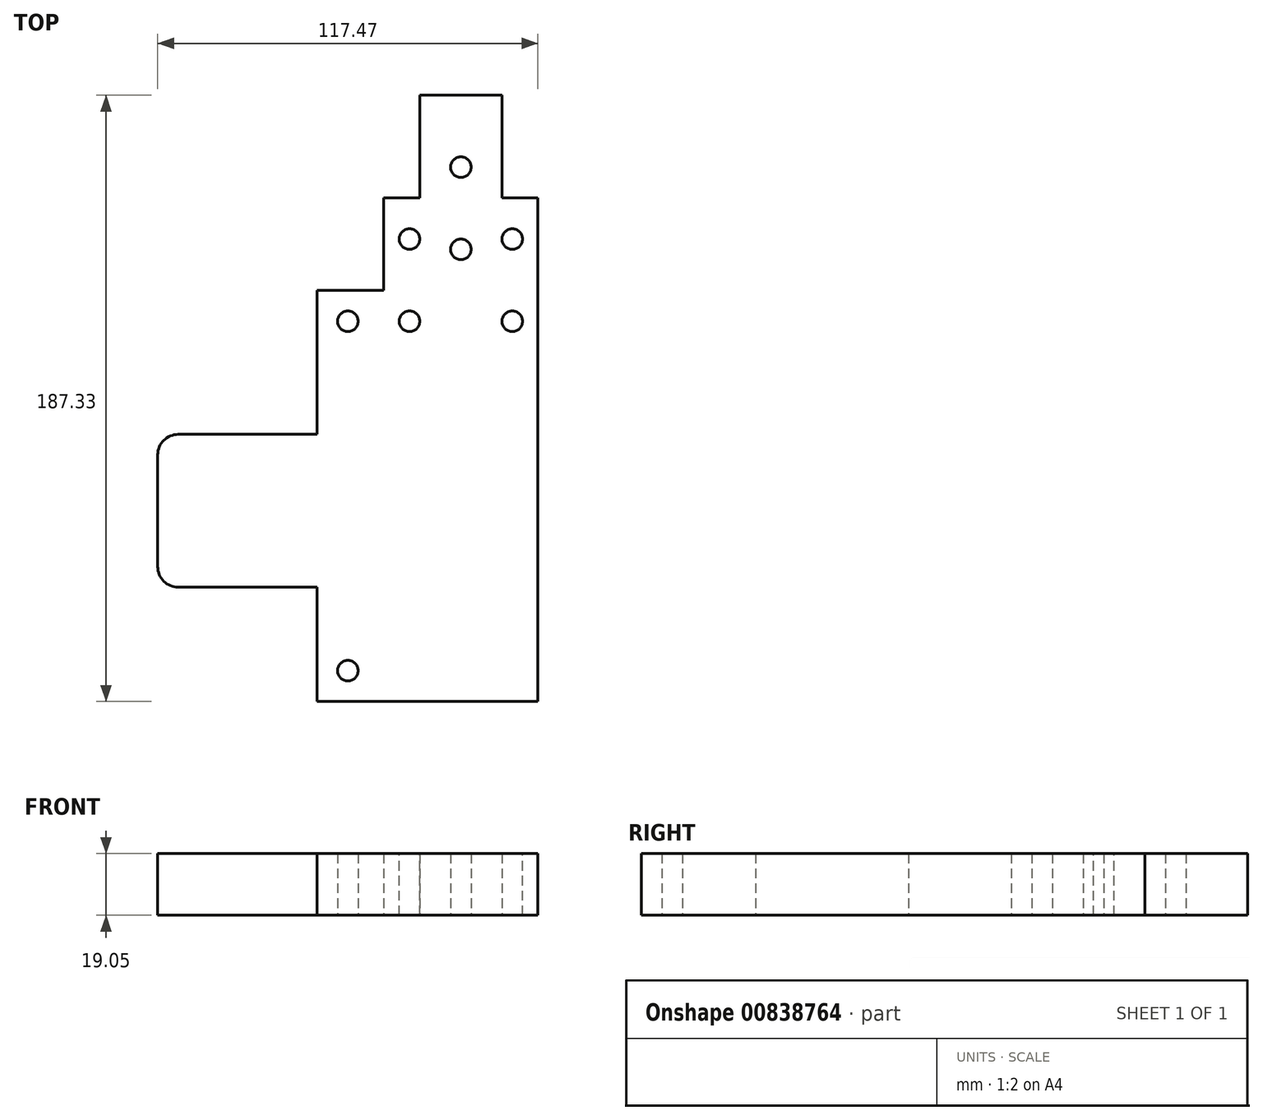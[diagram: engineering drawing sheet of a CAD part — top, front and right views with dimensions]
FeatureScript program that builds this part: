
annotation { "Feature Type Name" : "Feature", "Feature Type Description" : "" }
export const myFeature = defineFeature(function(context is Context, id is Id, definition is map)
    precondition{}
    {
        {
            var Q0;
            Q0=qCreatedBy(makeId("Top.planeOp"),FACE);
            var sketch = newSketch(context, id + "F0", { "sketchPlane" : qUnion([Q0])});
            skLineSegment(sketch, "E0", {"start": v(21.17, -220.11) * mm, "end": v(10.06, -220.11) * mm});
            skLineSegment(sketch, "E1", {"start": v(-26.45, -267.74) * mm, "end": v(-96.3, -267.74) * mm, "construction": true});
            skLineSegment(sketch, "E2", {"start": v(-96.3, -314.98) * mm, "end": v(-26.45, -314.98) * mm});
            skLineSegment(sketch, "E3", {"start": v(-26.45, -220.11) * mm, "end": v(-26.45, -248.69) * mm});
            skLineSegment(sketch, "E4", {"start": v(21.17, -220.11) * mm, "end": v(21.17, -375.69) * mm});
            skLineSegment(sketch, "E5", {"start": v(-26.45, -375.69) * mm, "end": v(21.17, -375.69) * mm});
            skLineSegment(sketch, "E6", {"start": v(-45.5, -340.38) * mm, "end": v(-45.5, -375.69) * mm, "construction": true});
            skLineSegment(sketch, "E7", {"start": v(-26.45, -362.99) * mm, "end": v(-13.75, -362.99) * mm, "construction": true});
            skLineSegment(sketch, "E8", {"start": v(-13.75, -375.69) * mm, "end": v(-13.75, -362.99) * mm});
            skLineSegment(sketch, "E9", {"start": v(-26.45, -350.29) * mm, "end": v(-39.15, -350.29) * mm});
            skLineSegment(sketch, "E10", {"start": v(-26.45, -375.69) * mm, "end": v(-47.09, -375.69) * mm});
            skLineSegment(sketch, "E11", {"start": v(-26.45, -362.99) * mm, "end": v(-26.45, -375.69) * mm});
            skLineSegment(sketch, "E12", {"start": v(-26.45, -340.38) * mm, "end": v(-26.45, -350.29) * mm});
            skLineSegment(sketch, "E13", {"start": v(-96.3, -293.14) * mm, "end": v(-96.3, -340.38) * mm});
            skPoint(sketch, "E14.visualSharp", {"position": v(-45.5, -350.29) * mm});
            skArc(sketch, "E14.filletArc", {"start": v(-39.15, -350.29) * mm, "mid": v(-43.64, -352.15) * mm, "end": v(-45.5, -356.64) * mm});
            skLineSegment(sketch, "E15.top", {"start": v(-15.34, -213.76) * mm, "end": v(10.06, -213.76) * mm, "construction": true});
            skLineSegment(sketch, "E15.left", {"start": v(-15.34, -220.11) * mm, "end": v(-15.34, -188.36) * mm});
            skLineSegment(sketch, "E15.right", {"start": v(10.06, -220.11) * mm, "end": v(10.06, -188.36) * mm});
            skLineSegment(sketch, "E16.trimOffspring", {"start": v(-15.34, -220.11) * mm, "end": v(-26.45, -220.11) * mm});
            skLineSegment(sketch, "E17.0", {"start": v(-96.3, -340.38) * mm, "end": v(-47.09, -340.38) * mm});
            skLineSegment(sketch, "E18.0", {"start": v(-26.45, -293.14) * mm, "end": v(-47.09, -293.14) * mm, "construction": true});
            skLineSegment(sketch, "E19.0", {"start": v(-15.34, -188.36) * mm, "end": v(10.06, -188.36) * mm});
            skCircle(sketch, "E20", {"center": v(-37.56, -366.16) * mm, "radius": 3.18 * mm});
            skLineSegment(sketch, "E21.0", {"start": v(-47.09, -242.34) * mm, "end": v(-47.09, -245.51) * mm, "construction": true});
            skLineSegment(sketch, "E22.0", {"start": v(-26.45, -242.34) * mm, "end": v(-47.09, -242.34) * mm, "construction": true});
            skLineSegment(sketch, "E23.trimOffspring", {"start": v(-47.09, -340.38) * mm, "end": v(-47.09, -375.69) * mm});
            skLineSegment(sketch, "E24", {"start": v(-47.09, -293.14) * mm, "end": v(-96.3, -293.14) * mm});
            skLineSegment(sketch, "E25", {"start": v(-26.45, -242.34) * mm, "end": v(-26.45, -293.14) * mm, "construction": true});
            skCircle(sketch, "E26", {"center": v(-37.56, -258.21) * mm, "radius": 3.18 * mm});
            skLineSegment(sketch, "E27.0", {"start": v(-26.45, -248.69) * mm, "end": v(-47.09, -248.69) * mm});
            skLineSegment(sketch, "E28", {"start": v(-47.09, -248.69) * mm, "end": v(-47.09, -293.14) * mm});
            skLineSegment(sketch, "E29", {"start": v(-47.09, -245.51) * mm, "end": v(-47.09, -248.69) * mm, "construction": true});
            skLineSegment(sketch, "E30.0", {"start": v(-15.34, -210.59) * mm, "end": v(-26.45, -210.59) * mm});
            skCircle(sketch, "E31", {"center": v(-2.64, -210.59) * mm, "radius": 3.18 * mm});
            skPoint(sketch, "E31.centerSnap0", {"position": v(-2.64, -188.36) * mm});
            skCircle(sketch, "E32.0.1.0", {"center": v(-2.64, -235.99) * mm, "radius": 3.18 * mm});
            skLineSegment(sketch, "E32.direction1", {"start": v(-2.64, -210.59) * mm, "end": v(22.76, -210.59) * mm, "construction": true});
            skLineSegment(sketch, "E32.direction2", {"start": v(-2.64, -210.59) * mm, "end": v(-2.64, -235.99) * mm, "construction": true});
            skSolve(sketch);
        }
        {
            var Q0;
            Q0=qSketchRegion(id+"F0",true);
            extrude(context, id + "F1", {"entities" : qUnion([Q0]), "depth" : 19.05 * mm, "offsetDistance" : 25.4 * mm});
        }
        {
            var Q0;
            Q0=makeQuery(id+"F1.opExtrude","CAP_FACE",FACE,{"disambiguationData":[OSD([sQuery(id+"F0.wireOp",EDGE,"E0"),sQuery(id+"F0.wireOp",EDGE,"E1"),sQuery(id+"F0.wireOp",EDGE,"E2"),sQuery(id+"F0.wireOp",EDGE,"E3"),sQuery(id+"F0.wireOp",EDGE,"E4"),sQuery(id+"F0.wireOp",EDGE,"E5"),sQuery(id+"F0.wireOp",EDGE,"E6"),sQuery(id+"F0.wireOp",EDGE,"E7"),sQuery(id+"F0.wireOp",EDGE,"E8"),sQuery(id+"F0.wireOp",EDGE,"E9"),sQuery(id+"F0.wireOp",EDGE,"E10"),sQuery(id+"F0.wireOp",EDGE,"E11"),sQuery(id+"F0.wireOp",EDGE,"E12"),sQuery(id+"F0.wireOp",EDGE,"E13"),sQuery(id+"F0.wireOp",EDGE,"E14.filletArc"),sQuery(id+"F0.wireOp",EDGE,"E15.top"),sQuery(id+"F0.wireOp",EDGE,"E15.left"),sQuery(id+"F0.wireOp",EDGE,"E15.right"),sQuery(id+"F0.wireOp",EDGE,"E16.trimOffspring")])],"isStart":false});
            var sketch = newSketch(context, id + "F2", { "sketchPlane" : qUnion([Q0])});
            skCircle(sketch, "E33", {"center": v(-18.51, -232.81) * mm, "radius": 3.18 * mm});
            skCircle(sketch, "E34.1.0.0", {"center": v(13.24, -232.81) * mm, "radius": 3.18 * mm});
            skLineSegment(sketch, "E34.direction1", {"start": v(-18.51, -232.81) * mm, "end": v(13.24, -232.81) * mm, "construction": true});
            skCircle(sketch, "E35.0.1.0", {"center": v(-18.51, -258.21) * mm, "radius": 3.18 * mm});
            skCircle(sketch, "E35.0.1.1", {"center": v(13.24, -258.21) * mm, "radius": 3.18 * mm});
            skLineSegment(sketch, "E35.direction1", {"start": v(-18.51, -232.81) * mm, "end": v(6.89, -232.81) * mm, "construction": true});
            skLineSegment(sketch, "E35.direction2", {"start": v(-18.51, -232.81) * mm, "end": v(-18.51, -258.21) * mm, "construction": true});
            skSolve(sketch);
        }
        {
            var Q0;
            Q0=makeQuery(id+"F2.imprint","IMPRINT",FACE,{"disambiguationData":[TD([[makeQuery(id+"F2.imprint","IMPRINT",EDGE,{"derivedFrom":sQuery(id+"F2.wireOp",EDGE,"E33")}),1.0]])]});
            var Q1;
            Q1=makeQuery(id+"F2.imprint","IMPRINT",FACE,{"disambiguationData":[TD([[makeQuery(id+"F2.imprint","IMPRINT",EDGE,{"derivedFrom":sQuery(id+"F2.wireOp",EDGE,"E34.1.0.0")}),1.0]])]});
            var Q2;
            Q2=makeQuery(id+"F2.imprint","IMPRINT",FACE,{"disambiguationData":[TD([[makeQuery(id+"F2.imprint","IMPRINT",EDGE,{"derivedFrom":sQuery(id+"F2.wireOp",EDGE,"E35.0.1.1")}),1.0]])]});
            var Q3;
            Q3=makeQuery(id+"F2.imprint","IMPRINT",FACE,{"disambiguationData":[TD([[makeQuery(id+"F2.imprint","IMPRINT",EDGE,{"derivedFrom":sQuery(id+"F2.wireOp",EDGE,"E35.0.1.0")}),1.0]])]});
            extrude(context, id + "F3", {"entities" : qUnion([Q0, Q1, Q2, Q3]), "operationType" : NewBodyOperationType.REMOVE, "oppositeDirection" : true, "depth" : 25.4 * mm, "offsetDistance" : 25.4 * mm});
        }
        {
            var Q0;
            Q0=makeQuery(id+"F1.opExtrude","SWEPT_EDGE",EDGE,{"disambiguationData":[OSD([sQuery(id+"F0.wireOp",EDGE,"E13"),sQuery(id+"F0.wireOp",EDGE,"E17.0")])]});
            var Q1;
            Q1=makeQuery(id+"F1.opExtrude","SWEPT_EDGE",EDGE,{"disambiguationData":[OSD([sQuery(id+"F0.wireOp",EDGE,"E13"),sQuery(id+"F0.wireOp",EDGE,"E18.0")])]});
            fillet(context, id + "F4", {"entities" : qUnion([Q0, Q1]), "radius" : 6.35 * mm, "tangentPropagation" : true, "allowEdgeOverflow" : false});
        }
    });
